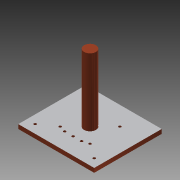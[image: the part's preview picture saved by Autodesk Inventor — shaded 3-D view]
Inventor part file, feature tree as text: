
AUTODESK INVENTOR PART (.ipt)
format: ipt  version: 2013 (Build 170138000, 138)  size: 130,048 bytes
history: native  units: mm
features: sketch x6, extrude x4, other x1, hole x1
ambient origin geometry x8: Origin, YZ Plane, XZ Plane, XY Plane, X Axis, Y Axis, Z Axis, Center Point
feature tree (12):
  other  "ソリッド1"
  extrude  "押し出し1"  Depth=5.0mm TaperAngle=0.0deg
  extrude  "押し出し2"  Depth=5.0mm TaperAngle=0.0deg
  extrude  "押し出し3"  Depth=5.0mm TaperAngle=0.0deg
  hole  "穴1"  [1 undecoded]
  sketch  "スケッチ5"
  sketch  "スケッチ6"
  extrude  "押し出し4"  Depth=10.0mm
  sketch  "スケッチ1"
  sketch  "スケッチ2"
  sketch  "スケッチ3"
  sketch  "スケッチ4"
note: 1 required parameter value undecoded (feature->parameter linkage not recoverable at this tier; creation-order binding heuristic only, values carry confidence <= 0.55)
